# Revit family: KG37 - Free Swing Transom Closer
name_source: partatom
category: Specialty Equipment
units: mm (PartAtom-declared; Revit-internal decimal feet)

## family parameters
Always vertical = No
Cut with Voids When Loaded = No
Part Type = Normal
Room Calculation Point = No
Round Connector Dimension = Use Diameter
Shared = No
Work Plane-Based = No

## types (1)
- KG37 - Free Swing Transom Closer
    AssetType = Fixed
    BIMObjectName = KingswayGroup_ControlledDoorClosers_FreeSwingTransomCloser
    Category = Pr_30_36_59_15:Controlled door closers
    Color = For full range of available finishes and colours, contact Kingsway Group
    Default Elevation = 0 mm  [stored 0 ft]
    Description = Double Action Transom Closer - Free Swing
    DurationUnit = year
    Features = Suitable for doors up to 300kg, the KG37 Free Swing Closer allows the door to open in both directions without resistance
    Finish = For full range of available finishes and colours, contact Kingsway Group
    IfcExportAs = IfcDiscreteAccessoryType
    IfcExportType = USERDEFINED
    Manufacturer = Kingsway Group
    ManufacturerName = Kingsway Group
    ManufacturerURL = https://kingswaygroupglobal.com
    Material = For full range of available material, contact Kingsway Group
    Model = KG37
    ModelNumber = KG37
    ModelReference = Free Swing Transom Closer
    Name = ControlledDoorClosers_FreeSwingTransomCloser_KG37_KingswayGroup
    NominalHeight = 43 mm  [stored 0.141076 ft]
    NominalLength = 344 mm  [stored 1.12861 ft]
    NominalWidth = 110 mm  [stored 0.360892 ft]
    PlateMaterial = NBS_Concept
    ProductInformation = https://kingswaygroupglobal.com
    Size = 344 x 43 x 110 mm
    URL = https://kingswaygroupglobal.com
    Uniclass2015Code = Pr_30_36_59_15
    Uniclass2015Title = Controlled door closers
    Uniclass2015Version = Products v1.36
    Version = 1
    WarrantyDescription = 5-Year Guarantee *For faulty manufacture and not for damage
    WarrantyDurationParts = 5
    WarrantyDurationUnit = year

note: [stored X ft] marks values corroborated as IEEE doubles in the binary element streams (Revit-internal decimal feet)

## geometry (parser evidence)
native form markers: Sweep x3
no freeform markers — native parametric forms only
